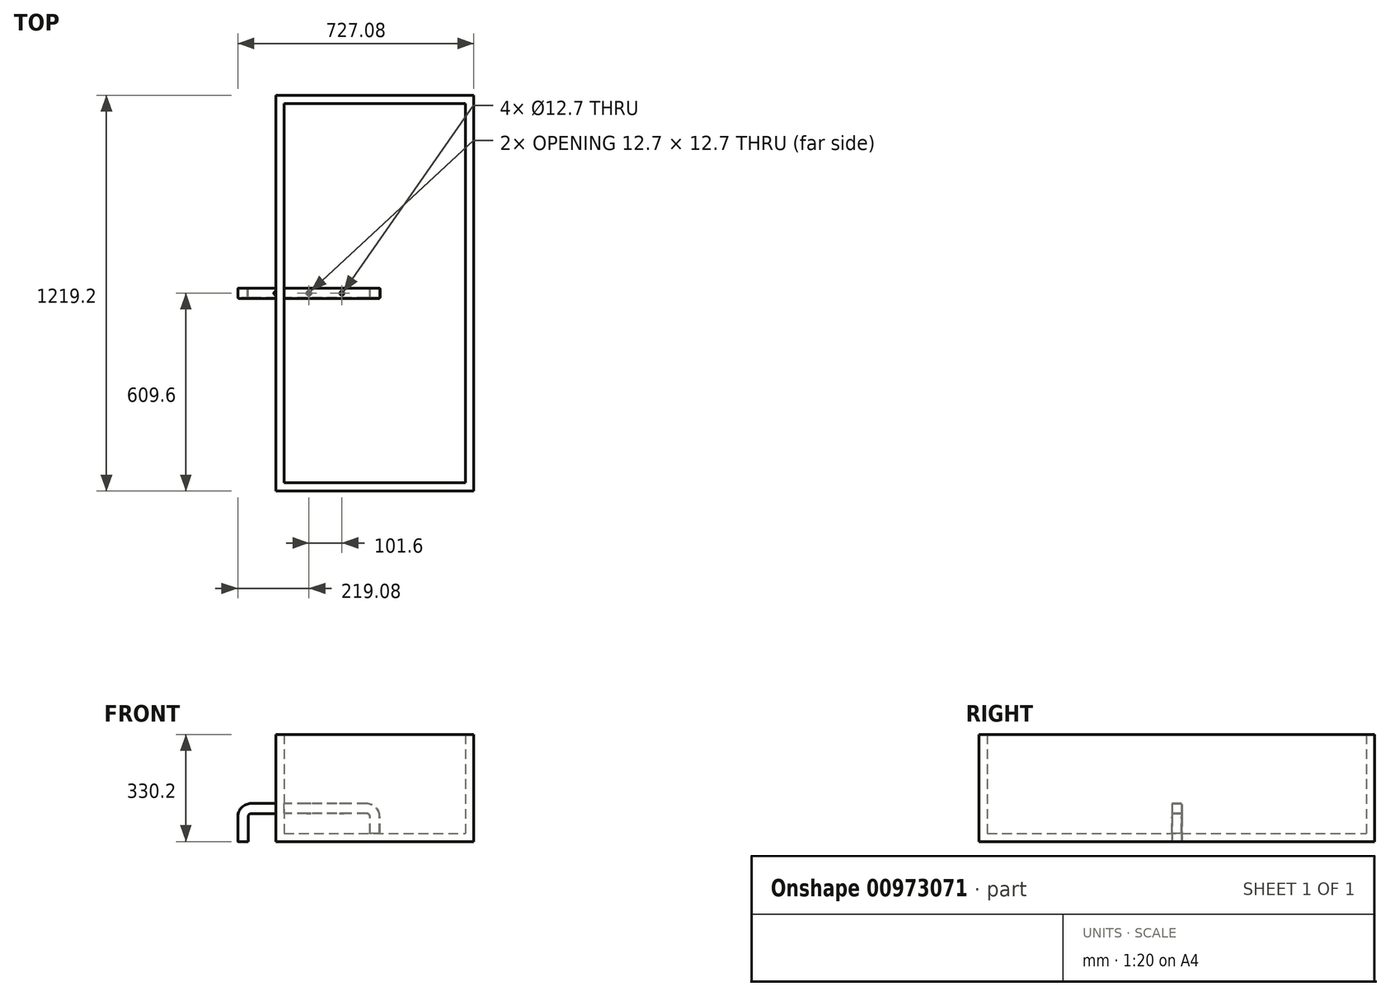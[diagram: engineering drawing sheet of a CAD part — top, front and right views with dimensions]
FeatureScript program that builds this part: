
annotation { "Feature Type Name" : "Feature", "Feature Type Description" : "" }
export const myFeature = defineFeature(function(context is Context, id is Id, definition is map)
    precondition{}
    {
        {
            var Q0;
            Q0=qCreatedBy(makeId("Top.planeOp"),FACE);
            var sketch = newSketch(context, id + "F0", { "sketchPlane" : qUnion([Q0])});
            skLineSegment(sketch, "E0.bottom", {"start": v(12.7, -15.88) * mm, "end": v(-12.7, -15.88) * mm});
            skLineSegment(sketch, "E0.top", {"start": v(12.7, 15.88) * mm, "end": v(-12.7, 15.88) * mm});
            skLineSegment(sketch, "E0.left", {"start": v(15.88, -12.7) * mm, "end": v(15.87, 12.7) * mm});
            skLineSegment(sketch, "E0.right", {"start": v(-15.87, -12.7) * mm, "end": v(-15.88, 12.7) * mm});
            skPoint(sketch, "E0.middle", {"position": v(0, 0) * mm});
            skPoint(sketch, "E1.visualSharp", {"position": v(-15.88, 15.88) * mm});
            skArc(sketch, "E1.filletArc", {"start": v(-12.7, 15.87) * mm, "mid": v(-14.95, 14.95) * mm, "end": v(-15.88, 12.7) * mm});
            skPoint(sketch, "E2.visualSharp", {"position": v(15.87, 15.88) * mm});
            skArc(sketch, "E2.filletArc", {"start": v(15.87, 12.7) * mm, "mid": v(14.95, 14.95) * mm, "end": v(12.7, 15.88) * mm});
            skPoint(sketch, "E3.visualSharp", {"position": v(15.88, -15.87) * mm});
            skArc(sketch, "E3.filletArc", {"start": v(12.7, -15.87) * mm, "mid": v(14.95, -14.95) * mm, "end": v(15.88, -12.7) * mm});
            skPoint(sketch, "E4.visualSharp", {"position": v(-15.87, -15.88) * mm});
            skArc(sketch, "E4.filletArc", {"start": v(-15.87, -12.7) * mm, "mid": v(-14.95, -14.95) * mm, "end": v(-12.7, -15.88) * mm});
            skLineSegment(sketch, "E5.0", {"start": v(12.7, 14.29) * mm, "end": v(-12.7, 14.29) * mm});
            skArc(sketch, "E5.1", {"start": v(14.29, 12.7) * mm, "mid": v(13.82, 13.82) * mm, "end": v(12.7, 14.29) * mm});
            skArc(sketch, "E5.2", {"start": v(-12.7, 14.29) * mm, "mid": v(-13.82, 13.82) * mm, "end": v(-14.29, 12.7) * mm});
            skLineSegment(sketch, "E5.3", {"start": v(14.29, -12.7) * mm, "end": v(14.29, 12.7) * mm});
            skLineSegment(sketch, "E5.4", {"start": v(-14.29, -12.7) * mm, "end": v(-14.29, 12.7) * mm});
            skArc(sketch, "E5.5", {"start": v(-14.29, -12.7) * mm, "mid": v(-13.82, -13.82) * mm, "end": v(-12.7, -14.29) * mm});
            skLineSegment(sketch, "E5.6", {"start": v(12.7, -14.29) * mm, "end": v(-12.7, -14.29) * mm});
            skArc(sketch, "E5.7", {"start": v(12.7, -14.29) * mm, "mid": v(13.82, -13.82) * mm, "end": v(14.29, -12.7) * mm});
            skSolve(sketch);
        }
        {
            var Q0;
            Q0=qCreatedBy(makeId("Front.planeOp"),FACE);
            var sketch = newSketch(context, id + "F1", { "sketchPlane" : qUnion([Q0])});
            skLineSegment(sketch, "E6", {"start": v(0, 0) * mm, "end": v(0, 76.2) * mm});
            skLineSegment(sketch, "E7", {"start": v(-406.4, 76.2) * mm, "end": v(-406.4, 0) * mm});
            skLineSegment(sketch, "E8", {"start": v(-25.4, 101.6) * mm, "end": v(-381, 101.6) * mm});
            skPoint(sketch, "E9.visualSharp", {"position": v(-406.4, 101.6) * mm});
            skArc(sketch, "E9.filletArc", {"start": v(-381, 101.6) * mm, "mid": v(-398.96, 94.16) * mm, "end": v(-406.4, 76.2) * mm});
            skPoint(sketch, "E10.visualSharp", {"position": v(0, 101.6) * mm});
            skArc(sketch, "E10.filletArc", {"start": v(0, 76.2) * mm, "mid": v(-7.44, 94.16) * mm, "end": v(-25.4, 101.6) * mm});
            skSolve(sketch);
        }
        {
            var Q0;
            Q0=makeQuery(id+"F0.imprint","IMPRINT",FACE,{"disambiguationData":[TD([[makeQuery(id+"F0.imprint","IMPRINT",EDGE,{"derivedFrom":sQuery(id+"F0.wireOp",EDGE,"E0.bottom")}),-1.0]])]});
            var Q1;
            Q1 = qSketchRegion(id + "F1", true);
            var Q2;
            Q2 = qConstructionFilter(qBodyType(qCreatedBy(id + "F1" ,EDGE), BodyType.WIRE), ConstructionObject.NO);
            sweep(context, id + "F2", {"profiles" : qUnion([Q0, Q1]), "path" : qUnion([Q2])});
        }
        {
            var Q0;
            Q0=makeQuery(id+"F2.opSweep","SWEPT_BODY",BODY,{"disambiguationData":[OSD([sQuery(id+"F0.wireOp",EDGE,"E0.bottom"),sQuery(id+"F0.wireOp",EDGE,"E0.top"),sQuery(id+"F0.wireOp",EDGE,"E0.left"),sQuery(id+"F0.wireOp",EDGE,"E0.right"),sQuery(id+"F0.wireOp",EDGE,"E1.filletArc"),sQuery(id+"F0.wireOp",EDGE,"E2.filletArc"),sQuery(id+"F0.wireOp",EDGE,"E3.filletArc"),sQuery(id+"F0.wireOp",EDGE,"E4.filletArc"),sQuery(id+"F0.wireOp",EDGE,"E5.0"),sQuery(id+"F0.wireOp",EDGE,"E5.1"),sQuery(id+"F0.wireOp",EDGE,"E5.2"),sQuery(id+"F0.wireOp",EDGE,"E5.3"),sQuery(id+"F0.wireOp",EDGE,"E5.4"),sQuery(id+"F0.wireOp",EDGE,"E5.5"),sQuery(id+"F0.wireOp",EDGE,"E5.6"),sQuery(id+"F0.wireOp",EDGE,"E5.7"),sQuery(id+"F1.wireOp",EDGE,"E7")])]});
            transform(context, id + "F3", {"entities" : qUnion([Q0]), "transformType" : TransformType.TRANSLATION_3D, "dx" : 0 * mm, "dy" : 0 * mm, "dz" : 0 * mm, "makeCopy" : true});
        }
        {
            var Q0;
            Q0=makeQuery(id+"F2.opSweep","SWEPT_FACE",FACE,{"disambiguationData":[OSD([sQuery(id+"F0.wireOp",EDGE,"E0.left"),sQuery(id+"F1.wireOp",EDGE,"E8")])]});
            var sketch = newSketch(context, id + "F4", { "sketchPlane" : qUnion([Q0])});
            skCircle(sketch, "E11", {"center": v(-304.8, 0) * mm, "radius": 6.35 * mm});
            skCircle(sketch, "E12", {"center": v(-101.6, 0) * mm, "radius": 6.35 * mm});
            skSolve(sketch);
        }
        {
            var Q0;
            Q0 = qSketchRegion(id + "F4", true);
            extrude(context, id + "F5", {"entities" : qUnion([Q0]), "operationType" : NewBodyOperationType.REMOVE, "endBound" : BoundingType.THROUGH_ALL, "oppositeDirection" : true, "depth" : 25.4 * mm, "offsetDistance" : 25.4 * mm});
        }
        {
            var Q0;
            Q0=makeQuery(id+"F3.opPattern","COPY",FACE,{"derivedFrom":makeQuery(id+"F2.opSweep","SWEPT_FACE",FACE,{"disambiguationData":[OSD([sQuery(id+"F0.wireOp",EDGE,"E0.left"),sQuery(id+"F1.wireOp",EDGE,"E8")])]}),"instanceName":"1"});
            var sketch = newSketch(context, id + "F6", { "sketchPlane" : qUnion([Q0])});
            skCircle(sketch, "E13", {"center": v(-203.2, 0) * mm, "radius": 6.35 * mm});
            skSolve(sketch);
        }
        {
            var Q0;
            Q0 = qSketchRegion(id + "F6", true);
            extrude(context, id + "F7", {"entities" : qUnion([Q0]), "operationType" : NewBodyOperationType.REMOVE, "endBound" : BoundingType.THROUGH_ALL, "oppositeDirection" : true, "depth" : 25.4 * mm, "offsetDistance" : 25.4 * mm});
        }
        {
            var Q0;
            Q0=qCreatedBy(makeId("Top.planeOp"),FACE);
            var sketch = newSketch(context, id + "F8", { "sketchPlane" : qUnion([Q0])});
            skLineSegment(sketch, "E14.bottom", {"start": v(-304.8, -609.6) * mm, "end": v(304.8, -609.6) * mm});
            skLineSegment(sketch, "E14.top", {"start": v(-304.8, 609.6) * mm, "end": v(304.8, 609.6) * mm});
            skLineSegment(sketch, "E14.left", {"start": v(-304.8, -609.6) * mm, "end": v(-304.8, 609.6) * mm});
            skLineSegment(sketch, "E14.right", {"start": v(304.8, -609.6) * mm, "end": v(304.8, 609.6) * mm});
            skPoint(sketch, "E14.middle", {"position": v(0, 0) * mm});
            skSolve(sketch);
        }
        {
            var Q0;
            Q0 = qSketchRegion(id + "F8", true);
            extrude(context, id + "F9", {"entities" : qUnion([Q0]), "depth" : 25.4 * mm, "offsetDistance" : 25.4 * mm});
        }
        {
            var Q0;
            Q0=makeQuery(id+"F9.opExtrude","CAP_FACE",FACE,{"disambiguationData":[OSD([sQuery(id+"F8.wireOp",EDGE,"E14.bottom"),sQuery(id+"F8.wireOp",EDGE,"E14.top"),sQuery(id+"F8.wireOp",EDGE,"E14.left"),sQuery(id+"F8.wireOp",EDGE,"E14.right")])],"isStart":false});
            var sketch = newSketch(context, id + "F10", { "sketchPlane" : qUnion([Q0])});
            skLineSegment(sketch, "E15.0", {"start": v(-279.4, 584.2) * mm, "end": v(279.4, 584.2) * mm});
            skLineSegment(sketch, "E15.1", {"start": v(-279.4, -584.2) * mm, "end": v(-279.4, 584.2) * mm});
            skLineSegment(sketch, "E15.2", {"start": v(-279.4, -584.2) * mm, "end": v(279.4, -584.2) * mm});
            skLineSegment(sketch, "E15.3", {"start": v(279.4, -584.2) * mm, "end": v(279.4, 584.2) * mm});
            skLineSegment(sketch, "E16.0", {"start": v(-304.8, -609.6) * mm, "end": v(-304.8, 609.6) * mm});
            skLineSegment(sketch, "E17.0", {"start": v(-304.8, 609.6) * mm, "end": v(304.8, 609.6) * mm});
            skLineSegment(sketch, "E18.0", {"start": v(304.8, -609.6) * mm, "end": v(304.8, 609.6) * mm});
            skLineSegment(sketch, "E19.0", {"start": v(-304.8, -609.6) * mm, "end": v(304.8, -609.6) * mm});
            skSolve(sketch);
        }
        {
            var Q0;
            Q0 = qSketchRegion(id + "F10", true);
            extrude(context, id + "F11", {"entities" : qUnion([Q0]), "operationType" : NewBodyOperationType.ADD, "depth" : 304.8 * mm, "offsetDistance" : 25.4 * mm});
        }
    });
